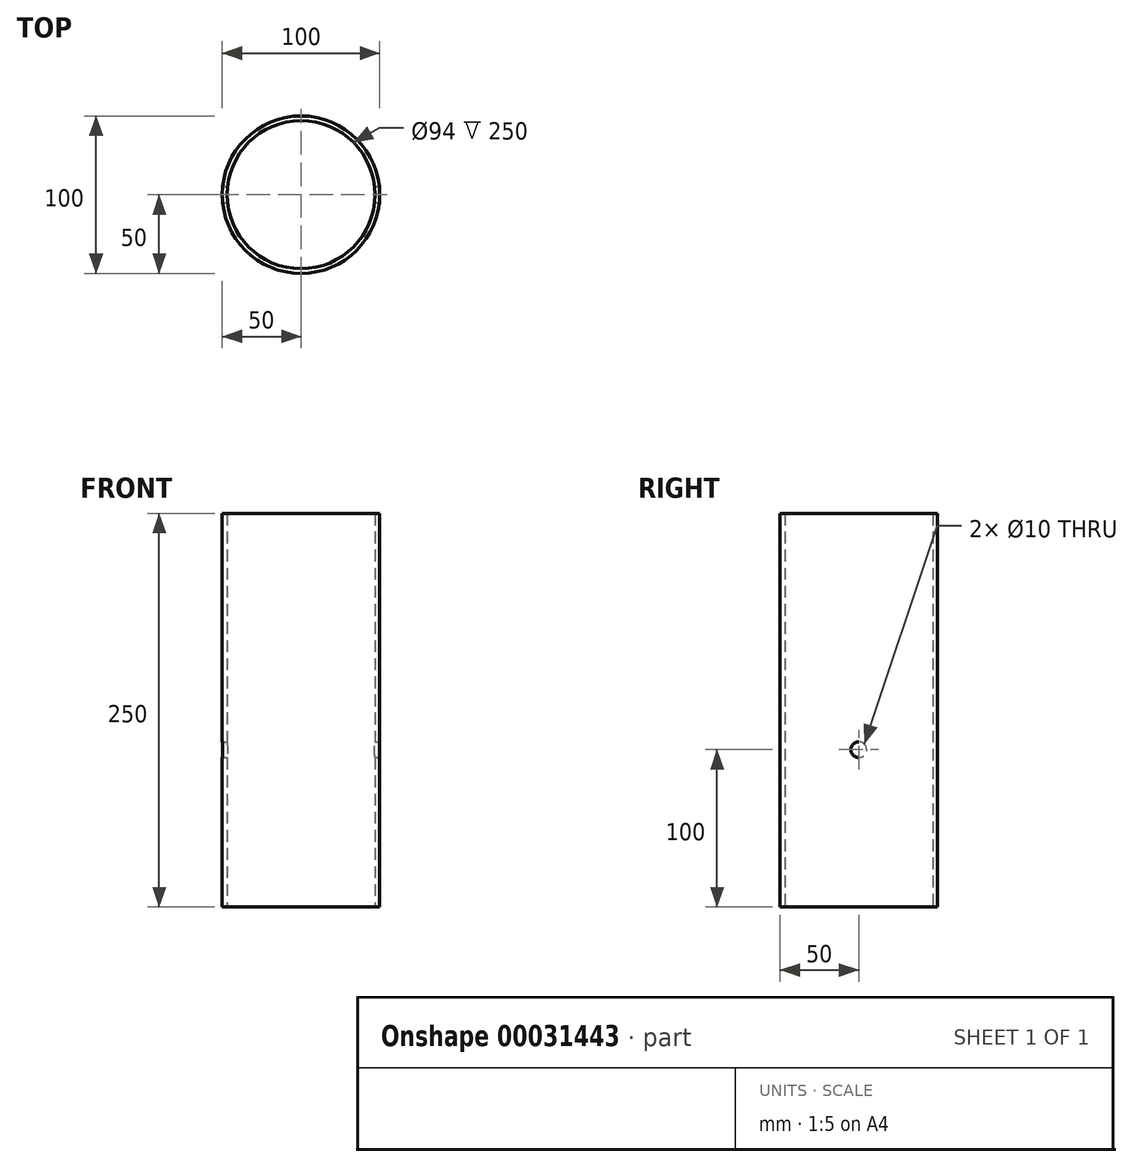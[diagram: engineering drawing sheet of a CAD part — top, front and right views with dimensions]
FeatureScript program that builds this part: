
annotation { "Feature Type Name" : "Feature", "Feature Type Description" : "" }
export const myFeature = defineFeature(function(context is Context, id is Id, definition is map)
    precondition{}
    {
        {
            var Q0;
            Q0=qCreatedBy(makeId("Top.planeOp"),FACE);
            var sketch = newSketch(context, id + "F0", { "sketchPlane" : qUnion([Q0])});
            skCircle(sketch, "E0", {"center": v(0, 0) * mm, "radius": 50 * mm});
            skCircle(sketch, "E1", {"center": v(0, 0) * mm, "radius": 47 * mm});
            skSolve(sketch);
        }
        {
            var Q0;
            Q0 = qSketchRegion(id + "F0", true);
            extrude(context, id + "F1", {"entities" : qUnion([Q0]), "depth" : 250 * mm});
        }
        {
            var Q0;
            Q0=qCreatedBy(makeId("Right.planeOp"),FACE);
            var sketch = newSketch(context, id + "F2", { "sketchPlane" : qUnion([Q0])});
            skCircle(sketch, "E2", {"center": v(0, 100) * mm, "radius": 5 * mm});
            skSolve(sketch);
        }
        {
            var Q0;
            Q0 = qSketchRegion(id + "F2", true);
            extrude(context, id + "F3", {"entities" : qUnion([Q0]), "operationType" : NewBodyOperationType.REMOVE, "endBound" : BoundingType.SYMMETRIC, "oppositeDirection" : true, "depth" : 200 * mm});
        }
    });
